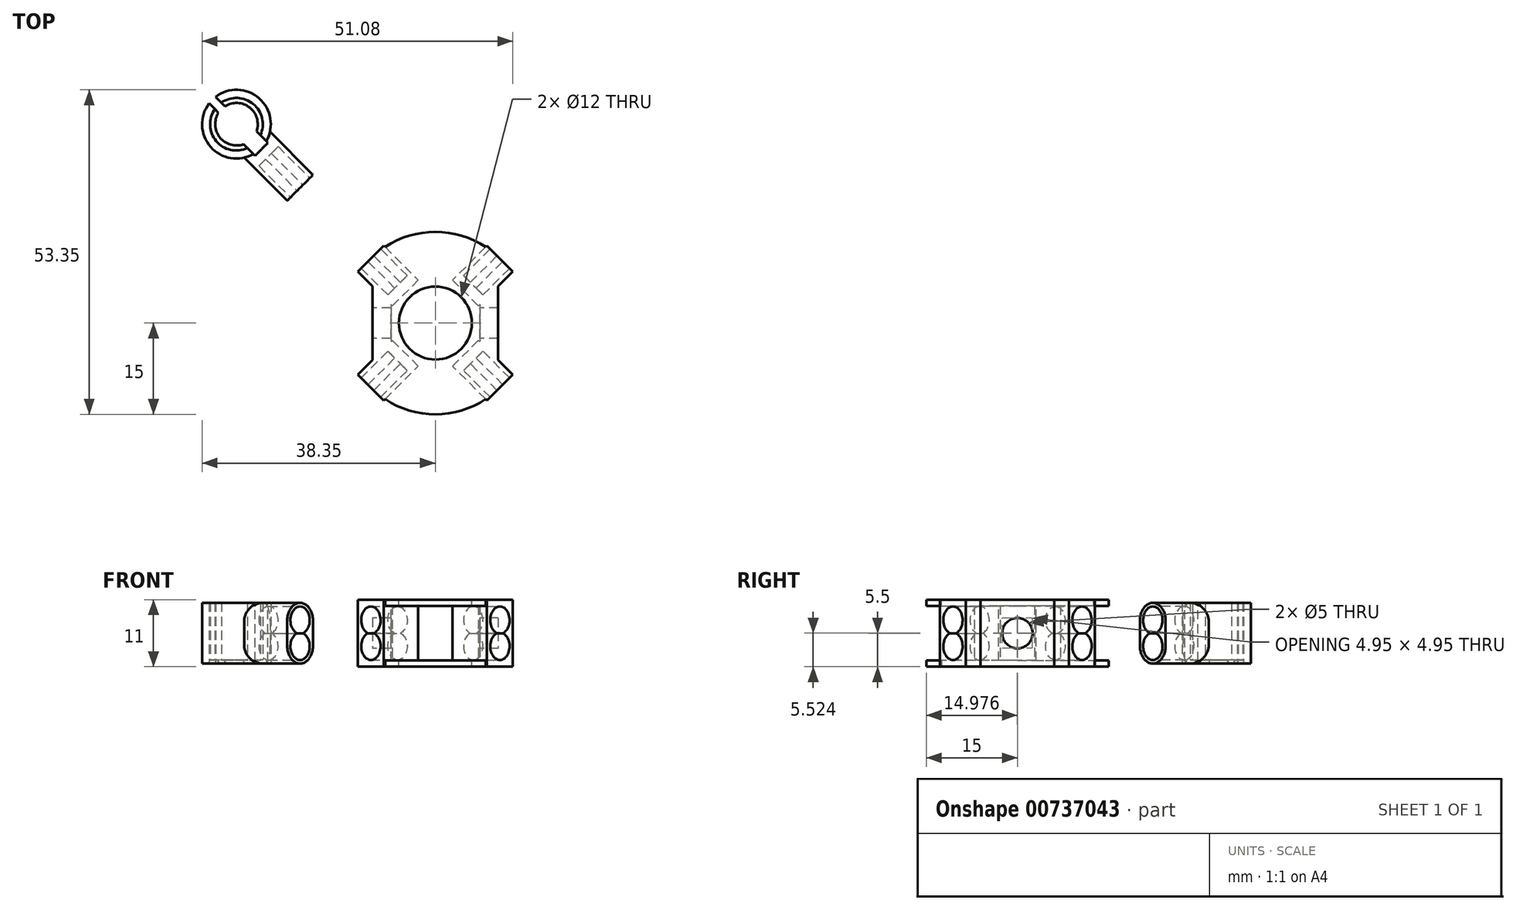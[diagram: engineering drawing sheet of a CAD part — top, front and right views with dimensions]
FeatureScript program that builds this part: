
annotation { "Feature Type Name" : "Feature", "Feature Type Description" : "" }
export const myFeature = defineFeature(function(context is Context, id is Id, definition is map)
    precondition{}
    {
        {
            var Q0;
            Q0=qCreatedBy(makeId("Top.planeOp"),FACE);
            var sketch = newSketch(context, id + "F0", { "sketchPlane" : qUnion([Q0])});
            skLineSegment(sketch, "E0", {"start": v(-32.7, -32.7) * mm, "end": v(32.7, 32.7) * mm});
            skLineSegment(sketch, "E1", {"start": v(-32.7, 32.7) * mm, "end": v(32.7, -32.7) * mm});
            skCircle(sketch, "E2", {"center": v(32.7, 32.7) * mm, "radius": 4.33 * mm});
            skCircle(sketch, "E3", {"center": v(32.7, -32.7) * mm, "radius": 4.33 * mm});
            skCircle(sketch, "E4", {"center": v(-32.7, -32.7) * mm, "radius": 4.33 * mm});
            skCircle(sketch, "E5", {"center": v(-32.7, 32.7) * mm, "radius": 4.33 * mm});
            skSolve(sketch);
        }
        {
            var Q0;
            Q0=qCreatedBy(makeId("Top.planeOp"),FACE);
            var sketch = newSketch(context, id + "F1", { "sketchPlane" : qUnion([Q0])});
            skLineSegment(sketch, "E6", {"start": v(8.49, 12.73) * mm, "end": v(2.83, 7.07) * mm});
            skLineSegment(sketch, "E7", {"start": v(2.83, 7.07) * mm, "end": v(7.07, 2.83) * mm});
            skLineSegment(sketch, "E8", {"start": v(8.49, 12.73) * mm, "end": v(12.73, 8.49) * mm});
            skLineSegment(sketch, "E9", {"start": v(12.73, 8.49) * mm, "end": v(7.07, 2.83) * mm});
            skLineSegment(sketch, "E10.MirrorCS", {"start": v(12.73, -8.49) * mm, "end": v(7.07, -2.83) * mm});
            skLineSegment(sketch, "E11.MirrorCS", {"start": v(8.49, -12.73) * mm, "end": v(12.73, -8.49) * mm});
            skLineSegment(sketch, "E12.MirrorCS", {"start": v(8.49, -12.73) * mm, "end": v(2.83, -7.07) * mm});
            skLineSegment(sketch, "E13.MirrorCS", {"start": v(2.83, -7.07) * mm, "end": v(7.07, -2.83) * mm});
            skLineSegment(sketch, "E14.MirrorCS", {"start": v(-2.83, -7.07) * mm, "end": v(-7.07, -2.83) * mm});
            skLineSegment(sketch, "E15.MirrorCS", {"start": v(-8.49, -12.73) * mm, "end": v(-2.83, -7.07) * mm});
            skLineSegment(sketch, "E16.MirrorCS", {"start": v(-8.49, -12.73) * mm, "end": v(-12.73, -8.49) * mm});
            skLineSegment(sketch, "E17.MirrorCS", {"start": v(-8.49, 12.73) * mm, "end": v(-2.83, 7.07) * mm});
            skLineSegment(sketch, "E18.MirrorCS", {"start": v(-2.83, 7.07) * mm, "end": v(-7.07, 2.83) * mm});
            skLineSegment(sketch, "E19.MirrorCS", {"start": v(-8.49, 12.73) * mm, "end": v(-12.73, 8.49) * mm});
            skLineSegment(sketch, "E20.MirrorCS", {"start": v(-12.73, -8.49) * mm, "end": v(-7.07, -2.83) * mm});
            skLineSegment(sketch, "E21.MirrorCS", {"start": v(-12.73, 8.49) * mm, "end": v(-7.07, 2.83) * mm});
            skCircle(sketch, "E22", {"center": v(0, 0) * mm, "radius": 15 * mm, "construction": true});
            skSolve(sketch);
        }
        {
            var Q0;
            Q0 = qSketchRegion(id + "F1", true);
            extrude(context, id + "F2", {"entities" : qUnion([Q0]), "endBound" : BoundingType.SYMMETRIC, "depth" : 11 * mm, "offsetDistance" : 25 * mm});
        }
        {
            var Q0;
            Q0=makeQuery(id+"F2.opExtrude","CAP_FACE",FACE,{"disambiguationData":[OSD([sQuery(id+"F1.wireOp",EDGE,"E6"),sQuery(id+"F1.wireOp",EDGE,"E7"),sQuery(id+"F1.wireOp",EDGE,"E8"),sQuery(id+"F1.wireOp",EDGE,"E9")])],"isStart":false});
            var sketch = newSketch(context, id + "F3", { "sketchPlane" : qUnion([Q0])});
            skCircle(sketch, "E23", {"center": v(0, 0) * mm, "radius": 15 * mm});
            skSolve(sketch);
        }
        {
            var Q0;
            Q0 = qSketchRegion(id + "F3", true);
            extrude(context, id + "F4", {"entities" : qUnion([Q0]), "operationType" : NewBodyOperationType.ADD, "oppositeDirection" : true, "depth" : 1 * mm, "offsetDistance" : 25 * mm});
        }
        {
            var Q0;
            Q0=qCreatedBy(makeId("Top.planeOp"),FACE);
            var sketch = newSketch(context, id + "F5", { "sketchPlane" : qUnion([Q0])});
            skLineSegment(sketch, "E24.bottom", {"start": v(-10.31, -6.07) * mm, "end": v(-7.31, -6.07) * mm});
            skLineSegment(sketch, "E24.top", {"start": v(-10.31, 6.07) * mm, "end": v(-7.31, 6.07) * mm});
            skLineSegment(sketch, "E24.left", {"start": v(-10.31, -6.07) * mm, "end": v(-10.31, 6.07) * mm});
            skLineSegment(sketch, "E24.right", {"start": v(-7.31, -6.07) * mm, "end": v(-7.31, 6.07) * mm});
            skLineSegment(sketch, "E25.MirrorCS", {"start": v(10.31, -6.07) * mm, "end": v(7.31, -6.07) * mm});
            skLineSegment(sketch, "E26.MirrorCS", {"start": v(10.31, 6.07) * mm, "end": v(7.31, 6.07) * mm});
            skLineSegment(sketch, "E27.MirrorCS", {"start": v(7.31, -6.07) * mm, "end": v(7.31, 6.07) * mm});
            skLineSegment(sketch, "E28.MirrorCS", {"start": v(10.31, -6.07) * mm, "end": v(10.31, 6.07) * mm});
            skSolve(sketch);
        }
        {
            var Q0;
            Q0 = qSketchRegion(id + "F5", true);
            extrude(context, id + "F6", {"entities" : qUnion([Q0]), "operationType" : NewBodyOperationType.ADD, "endBound" : BoundingType.SYMMETRIC, "depth" : 10 * mm, "offsetDistance" : 25 * mm});
        }
        {
            var Q0;
            Q0=makeQuery(id+"F6.boolean.opBoolean","MERGE",FACE,{"derivedFrom":[makeQuery(id+"F2.opExtrude","CAP_FACE",FACE,{"disambiguationData":[OSD([sQuery(id+"F1.wireOp",EDGE,"E14.MirrorCS"),sQuery(id+"F1.wireOp",EDGE,"E15.MirrorCS"),sQuery(id+"F1.wireOp",EDGE,"E16.MirrorCS"),sQuery(id+"F1.wireOp",EDGE,"E20.MirrorCS")])],"isStart":true}),makeQuery(id+"F2.opExtrude","CAP_FACE",FACE,{"disambiguationData":[OSD([sQuery(id+"F1.wireOp",EDGE,"E17.MirrorCS"),sQuery(id+"F1.wireOp",EDGE,"E18.MirrorCS"),sQuery(id+"F1.wireOp",EDGE,"E19.MirrorCS"),sQuery(id+"F1.wireOp",EDGE,"E21.MirrorCS")])],"isStart":true}),makeQuery(id+"F6.opExtrude","CAP_FACE",FACE,{"disambiguationData":[OSD([sQuery(id+"F5.wireOp",EDGE,"E24.bottom"),sQuery(id+"F5.wireOp",EDGE,"E24.top"),sQuery(id+"F5.wireOp",EDGE,"E24.left"),sQuery(id+"F5.wireOp",EDGE,"E24.right")])],"isStart":true})]});
            var sketch = newSketch(context, id + "F7", { "sketchPlane" : qUnion([Q0])});
            skCircle(sketch, "E29", {"center": v(0, 0) * mm, "radius": 15 * mm});
            skSolve(sketch);
        }
        {
            var Q0;
            Q0 = qSketchRegion(id + "F7", true);
            extrude(context, id + "F8", {"entities" : qUnion([Q0]), "operationType" : NewBodyOperationType.ADD, "oppositeDirection" : true, "depth" : 1 * mm, "offsetDistance" : 25 * mm});
        }
        {
            var Q0;
            Q0=qCreatedBy(makeId("Top.planeOp"),FACE);
            var sketch = newSketch(context, id + "F9", { "sketchPlane" : qUnion([Q0])});
            skCircle(sketch, "E30", {"center": v(0, 0) * mm, "radius": 6 * mm});
            skSolve(sketch);
        }
        {
            var Q0;
            Q0 = qSketchRegion(id + "F9", true);
            extrude(context, id + "F10", {"entities" : qUnion([Q0]), "operationType" : NewBodyOperationType.REMOVE, "endBound" : BoundingType.SYMMETRIC, "oppositeDirection" : true, "depth" : 25 * mm, "offsetDistance" : 25 * mm});
        }
        {
            var Q0;
            Q0=makeQuery(id+"F2.opExtrude","SWEPT_FACE",FACE,{"disambiguationData":[OSD([sQuery(id+"F1.wireOp",EDGE,"E8")])]});
            var sketch = newSketch(context, id + "F11", { "sketchPlane" : qUnion([Q0])});
            skArc(sketch, "E31", {"start": v(0.66, 0) * mm, "mid": v(0, 4.4) * mm, "end": v(-0.66, 0) * mm});
            skArc(sketch, "E32", {"start": v(-0.66, 0) * mm, "mid": v(0, -4.4) * mm, "end": v(0.66, 0) * mm});
            skSolve(sketch);
        }
        {
            var Q0;
            Q0 = qSketchRegion(id + "F11", true);
            extrude(context, id + "F12", {"entities" : qUnion([Q0]), "operationType" : NewBodyOperationType.REMOVE, "oppositeDirection" : true, "depth" : 100 * mm, "offsetDistance" : 25 * mm});
        }
        {
            var Q0;
            Q0=makeQuery(id+"F2.opExtrude","SWEPT_FACE",FACE,{"disambiguationData":[OSD([sQuery(id+"F1.wireOp",EDGE,"E19.MirrorCS")])]});
            var sketch = newSketch(context, id + "F13", { "sketchPlane" : qUnion([Q0])});
            skArc(sketch, "E33", {"start": v(0.66, 0) * mm, "mid": v(0, 4.4) * mm, "end": v(-0.66, 0) * mm});
            skArc(sketch, "E34", {"start": v(-0.66, 0) * mm, "mid": v(0, -4.4) * mm, "end": v(0.66, 0) * mm});
            skSolve(sketch);
        }
        {
            var Q0;
            Q0 = qSketchRegion(id + "F13", true);
            extrude(context, id + "F14", {"entities" : qUnion([Q0]), "operationType" : NewBodyOperationType.REMOVE, "oppositeDirection" : true, "depth" : 100 * mm, "offsetDistance" : 25 * mm});
        }
        {
            var Q0;
            Q0=makeQuery(id+"F6.opExtrude","SWEPT_FACE",FACE,{"disambiguationData":[OSD([sQuery(id+"F5.wireOp",EDGE,"E24.left")])]});
            var sketch = newSketch(context, id + "F15", { "sketchPlane" : qUnion([Q0])});
            skCircle(sketch, "E35", {"center": v(0, 0) * mm, "radius": 2.5 * mm});
            skSolve(sketch);
        }
        {
            var Q0;
            Q0 = qSketchRegion(id + "F15", true);
            extrude(context, id + "F16", {"entities" : qUnion([Q0]), "operationType" : NewBodyOperationType.REMOVE, "oppositeDirection" : true, "depth" : 100 * mm, "offsetDistance" : 25 * mm});
        }
        {
            var Q0;
            Q0=makeQuery(id+"F14.boolean.opBoolean","SPLIT",FACE,{"disambiguationData":[TD([makeQuery(id+"F2.opExtrude","SWEPT_FACE",FACE,{"disambiguationData":[OSD([sQuery(id+"F1.wireOp",EDGE,"E12.MirrorCS")])]})])],"derivedFrom":makeQuery(id+"F2.opExtrude","SWEPT_FACE",FACE,{"disambiguationData":[OSD([sQuery(id+"F1.wireOp",EDGE,"E13.MirrorCS")])]})});
            var sketch = newSketch(context, id + "F17", { "sketchPlane" : qUnion([Q0])});
            skLineSegment(sketch, "E36.bottom", {"start": v(3, 5.5) * mm, "end": v(-3, 5.5) * mm});
            skLineSegment(sketch, "E36.top", {"start": v(3, -5.5) * mm, "end": v(-3, -5.5) * mm});
            skLineSegment(sketch, "E36.left", {"start": v(3, 5.5) * mm, "end": v(3, -5.5) * mm});
            skLineSegment(sketch, "E36.right", {"start": v(-3, 5.5) * mm, "end": v(-3, -5.5) * mm});
            skSolve(sketch);
        }
        {
            var Q0;
            Q0 = qSketchRegion(id + "F17", true);
            extrude(context, id + "F18", {"entities" : qUnion([Q0]), "operationType" : NewBodyOperationType.ADD, "oppositeDirection" : true, "depth" : 1.8 * mm, "offsetDistance" : 25 * mm});
        }
        {
            var Q0;
            Q0=makeQuery(id+"F14.boolean.opBoolean","SPLIT",FACE,{"disambiguationData":[TD([makeQuery(id+"F2.opExtrude","SWEPT_FACE",FACE,{"disambiguationData":[OSD([sQuery(id+"F1.wireOp",EDGE,"E17.MirrorCS")])]})])],"derivedFrom":makeQuery(id+"F2.opExtrude","SWEPT_FACE",FACE,{"disambiguationData":[OSD([sQuery(id+"F1.wireOp",EDGE,"E18.MirrorCS")])]})});
            var sketch = newSketch(context, id + "F19", { "sketchPlane" : qUnion([Q0])});
            skLineSegment(sketch, "E37.bottom", {"start": v(3, 4.5) * mm, "end": v(-3, 4.5) * mm});
            skLineSegment(sketch, "E37.top", {"start": v(3, -4.5) * mm, "end": v(-3, -4.5) * mm});
            skLineSegment(sketch, "E37.left", {"start": v(3, 4.5) * mm, "end": v(3, -4.5) * mm});
            skLineSegment(sketch, "E37.right", {"start": v(-3, 4.5) * mm, "end": v(-3, -4.5) * mm});
            skSolve(sketch);
        }
        {
            var Q0;
            Q0 = qSketchRegion(id + "F19", true);
            extrude(context, id + "F20", {"entities" : qUnion([Q0]), "operationType" : NewBodyOperationType.ADD, "oppositeDirection" : true, "depth" : 1.8 * mm, "offsetDistance" : 25 * mm});
        }
        {
            var Q0;
            Q0=makeQuery(id+"F12.boolean.opBoolean","SPLIT",FACE,{"disambiguationData":[TD([makeQuery(id+"F2.opExtrude","SWEPT_FACE",FACE,{"disambiguationData":[OSD([sQuery(id+"F1.wireOp",EDGE,"E15.MirrorCS")])]})])],"derivedFrom":makeQuery(id+"F2.opExtrude","SWEPT_FACE",FACE,{"disambiguationData":[OSD([sQuery(id+"F1.wireOp",EDGE,"E14.MirrorCS")])]})});
            var sketch = newSketch(context, id + "F21", { "sketchPlane" : qUnion([Q0])});
            skLineSegment(sketch, "E38.bottom", {"start": v(-3, 4.5) * mm, "end": v(3, 4.5) * mm});
            skLineSegment(sketch, "E38.top", {"start": v(-3, -4.5) * mm, "end": v(3, -4.5) * mm});
            skLineSegment(sketch, "E38.left", {"start": v(-3, 4.5) * mm, "end": v(-3, -4.5) * mm});
            skLineSegment(sketch, "E38.right", {"start": v(3, 4.5) * mm, "end": v(3, -4.5) * mm});
            skSolve(sketch);
        }
        {
            var Q0;
            Q0 = qSketchRegion(id + "F21", true);
            extrude(context, id + "F22", {"entities" : qUnion([Q0]), "operationType" : NewBodyOperationType.ADD, "oppositeDirection" : true, "depth" : 1.8 * mm, "offsetDistance" : 25 * mm});
        }
        {
            var Q0;
            Q0=makeQuery(id+"F12.boolean.opBoolean","SPLIT",FACE,{"disambiguationData":[TD([makeQuery(id+"F2.opExtrude","SWEPT_FACE",FACE,{"disambiguationData":[OSD([sQuery(id+"F1.wireOp",EDGE,"E6")])]})])],"derivedFrom":makeQuery(id+"F2.opExtrude","SWEPT_FACE",FACE,{"disambiguationData":[OSD([sQuery(id+"F1.wireOp",EDGE,"E7")])]})});
            var sketch = newSketch(context, id + "F23", { "sketchPlane" : qUnion([Q0])});
            skLineSegment(sketch, "E39.bottom", {"start": v(-3, -4.5) * mm, "end": v(3, -4.5) * mm});
            skLineSegment(sketch, "E39.top", {"start": v(-3, 4.5) * mm, "end": v(3, 4.5) * mm});
            skLineSegment(sketch, "E39.left", {"start": v(-3, -4.5) * mm, "end": v(-3, 4.5) * mm});
            skLineSegment(sketch, "E39.right", {"start": v(3, -4.5) * mm, "end": v(3, 4.5) * mm});
            skSolve(sketch);
        }
        {
            var Q0;
            Q0 = qSketchRegion(id + "F23", true);
            extrude(context, id + "F24", {"entities" : qUnion([Q0]), "operationType" : NewBodyOperationType.ADD, "oppositeDirection" : true, "depth" : 1.8 * mm, "offsetDistance" : 25 * mm});
        }
        {
            var Q0;
            Q0=qCreatedBy(makeId("Top.planeOp"),FACE);
            var sketch = newSketch(context, id + "F25", { "sketchPlane" : qUnion([Q0])});
            skCircle(sketch, "E40", {"center": v(-32.7, 32.7) * mm, "radius": 5.65 * mm});
            skCircle(sketch, "E41", {"center": v(-32.7, 32.7) * mm, "radius": 4.33 * mm});
            skSolve(sketch);
        }
        {
            var Q0;
            Q0 = qSketchRegion(id + "F25", true);
            extrude(context, id + "F26", {"entities" : qUnion([Q0]), "endBound" : BoundingType.SYMMETRIC, "depth" : 10 * mm, "offsetDistance" : 25 * mm});
        }
        {
            var Q0;
            Q0=qCreatedBy(makeId("Top.planeOp"),FACE);
            var sketch = newSketch(context, id + "F27", { "sketchPlane" : qUnion([Q0])});
            skLineSegment(sketch, "E42", {"start": v(-31.44, 27.2) * mm, "end": v(-24.37, 20.13) * mm});
            skLineSegment(sketch, "E43", {"start": v(-24.37, 20.13) * mm, "end": v(-20.13, 24.37) * mm});
            skLineSegment(sketch, "E44", {"start": v(-20.13, 24.37) * mm, "end": v(-27.2, 31.44) * mm});
            skLineSegment(sketch, "E45", {"start": v(-27.2, 31.44) * mm, "end": v(-31.44, 27.2) * mm});
            skSolve(sketch);
        }
        {
            var Q0;
            Q0 = qSketchRegion(id + "F27", true);
            extrude(context, id + "F28", {"entities" : qUnion([Q0]), "operationType" : NewBodyOperationType.ADD, "endBound" : BoundingType.SYMMETRIC, "depth" : 10 * mm, "offsetDistance" : 25 * mm});
        }
        {
            var Q0;
            Q0=qCreatedBy(makeId("Top.planeOp"),FACE);
            var sketch = newSketch(context, id + "F29", { "sketchPlane" : qUnion([Q0])});
            skLineSegment(sketch, "E46", {"start": v(-31.77, 29.65) * mm, "end": v(-29.65, 27.52) * mm});
            skLineSegment(sketch, "E47", {"start": v(-29.65, 27.52) * mm, "end": v(-27.52, 29.65) * mm});
            skLineSegment(sketch, "E48", {"start": v(-27.52, 29.65) * mm, "end": v(-29.65, 31.77) * mm});
            skLineSegment(sketch, "E49", {"start": v(-29.65, 31.77) * mm, "end": v(-31.77, 29.65) * mm});
            skSolve(sketch);
        }
        {
            var Q0;
            Q0=qCreatedBy(makeId("Top.planeOp"),FACE);
            var sketch = newSketch(context, id + "F30", { "sketchPlane" : qUnion([Q0])});
            skLineSegment(sketch, "E50", {"start": v(-35.65, 34.6) * mm, "end": v(-38.24, 37.18) * mm});
            skLineSegment(sketch, "E51", {"start": v(-38.24, 37.18) * mm, "end": v(-37.18, 38.24) * mm});
            skLineSegment(sketch, "E52", {"start": v(-37.18, 38.24) * mm, "end": v(-34.6, 35.65) * mm});
            skLineSegment(sketch, "E53", {"start": v(-34.6, 35.65) * mm, "end": v(-35.65, 34.6) * mm});
            skSolve(sketch);
        }
        {
            var Q0;
            Q0=makeQuery(id+"F28.boolean.opBoolean","MERGE",FACE,{"derivedFrom":[makeQuery(id+"F26.opExtrude","CAP_FACE",FACE,{"disambiguationData":[OSD([sQuery(id+"F25.wireOp",EDGE,"E40"),sQuery(id+"F25.wireOp",EDGE,"E41")])],"isStart":true}),makeQuery(id+"F28.opExtrude","CAP_FACE",FACE,{"disambiguationData":[OSD([sQuery(id+"F27.wireOp",EDGE,"E42"),sQuery(id+"F27.wireOp",EDGE,"E43"),sQuery(id+"F27.wireOp",EDGE,"E44"),sQuery(id+"F27.wireOp",EDGE,"E45")])],"isStart":true})]});
            var sketch = newSketch(context, id + "F31", { "sketchPlane" : qUnion([Q0])});
            skCircle(sketch, "E54", {"center": v(-32.7, -32.7) * mm, "radius": 5.65 * mm});
            skCircle(sketch, "E55", {"center": v(-32.7, -32.7) * mm, "radius": 3.5 * mm});
            skSolve(sketch);
        }
        {
            var Q0;
            Q0 = qSketchRegion(id + "F31", true);
            extrude(context, id + "F32", {"entities" : qUnion([Q0]), "operationType" : NewBodyOperationType.ADD, "oppositeDirection" : true, "depth" : 0.6 * mm, "offsetDistance" : 25 * mm});
        }
        {
            var Q0;
            Q0 = qSketchRegion(id + "F30", true);
            var Q1;
            Q1 = qSketchRegion(id + "F29", true);
            extrude(context, id + "F33", {"entities" : qUnion([Q0, Q1]), "operationType" : NewBodyOperationType.REMOVE, "endBound" : BoundingType.SYMMETRIC, "oppositeDirection" : true, "depth" : 25 * mm, "offsetDistance" : 25 * mm});
        }
        {
            var Q0;
            Q0=makeQuery(id+"F28.opExtrude","SWEPT_FACE",FACE,{"disambiguationData":[OSD([sQuery(id+"F27.wireOp",EDGE,"E43")])]});
            var sketch = newSketch(context, id + "F34", { "sketchPlane" : qUnion([Q0])});
            skArc(sketch, "E56", {"start": v(0.66, 0) * mm, "mid": v(0, 4.4) * mm, "end": v(-0.66, 0) * mm});
            skArc(sketch, "E57", {"start": v(-0.66, 0) * mm, "mid": v(0, -4.4) * mm, "end": v(0.66, 0) * mm});
            skSolve(sketch);
        }
        {
            var Q0;
            Q0 = qSketchRegion(id + "F34", true);
            extrude(context, id + "F35", {"entities" : qUnion([Q0]), "operationType" : NewBodyOperationType.REMOVE, "oppositeDirection" : true, "depth" : 7.34 * mm, "offsetDistance" : 25 * mm});
        }
        {
            var Q0;
            Q0=makeQuery(id+"F28.opExtrude","CAP_EDGE",EDGE,{"disambiguationData":[OSD([sQuery(id+"F27.wireOp",EDGE,"E44")])],"isStart":false});
            var Q1;
            Q1=makeQuery(id+"F28.opExtrude","CAP_EDGE",EDGE,{"disambiguationData":[OSD([sQuery(id+"F27.wireOp",EDGE,"E42")])],"isStart":false});
            var Q2;
            Q2=makeQuery(id+"F28.opExtrude","CAP_EDGE",EDGE,{"disambiguationData":[OSD([sQuery(id+"F27.wireOp",EDGE,"E44")])],"isStart":true});
            var Q3;
            Q3=makeQuery(id+"F28.opExtrude","CAP_EDGE",EDGE,{"disambiguationData":[OSD([sQuery(id+"F27.wireOp",EDGE,"E42")])],"isStart":true});
            fillet(context, id + "F36", {"entities" : qUnion([Q0, Q1, Q2, Q3]), "radius" : 3 * mm, "tangentPropagation" : true, "allowEdgeOverflow" : false});
        }
        {
            var Q0;
            {var subQ0=sQuery(id+"F7.wireOp",EDGE,"E29");Q0=makeQuery(id+"F8.boolean.opBoolean","SPLIT",FACE,{"disambiguationData":[TD([makeQuery(id+"F6.opExtrude","SWEPT_FACE",FACE,{"disambiguationData":[OSD([sQuery(id+"F5.wireOp",EDGE,"E24.left")])]})])],"derivedFrom":makeQuery(id+"F8.opExtrude","CAP_FACE",FACE,{"disambiguationData":[OSD([subQ0])],"isStart":false})});}
            var Q1;
            {var subQ0=sQuery(id+"F7.wireOp",EDGE,"E29");Q1=makeQuery(id+"F8.boolean.opBoolean","SPLIT",FACE,{"disambiguationData":[TD([makeQuery(id+"F6.opExtrude","SWEPT_FACE",FACE,{"disambiguationData":[OSD([sQuery(id+"F5.wireOp",EDGE,"E28.MirrorCS")])]})])],"derivedFrom":makeQuery(id+"F8.opExtrude","CAP_FACE",FACE,{"disambiguationData":[OSD([subQ0])],"isStart":false})});}
            extrude(context, id + "F37", {"entities" : qUnion([Q0, Q1]), "operationType" : NewBodyOperationType.REMOVE, "endBound" : BoundingType.SYMMETRIC, "oppositeDirection" : true, "depth" : 25 * mm, "offsetDistance" : 25 * mm});
        }
    });
